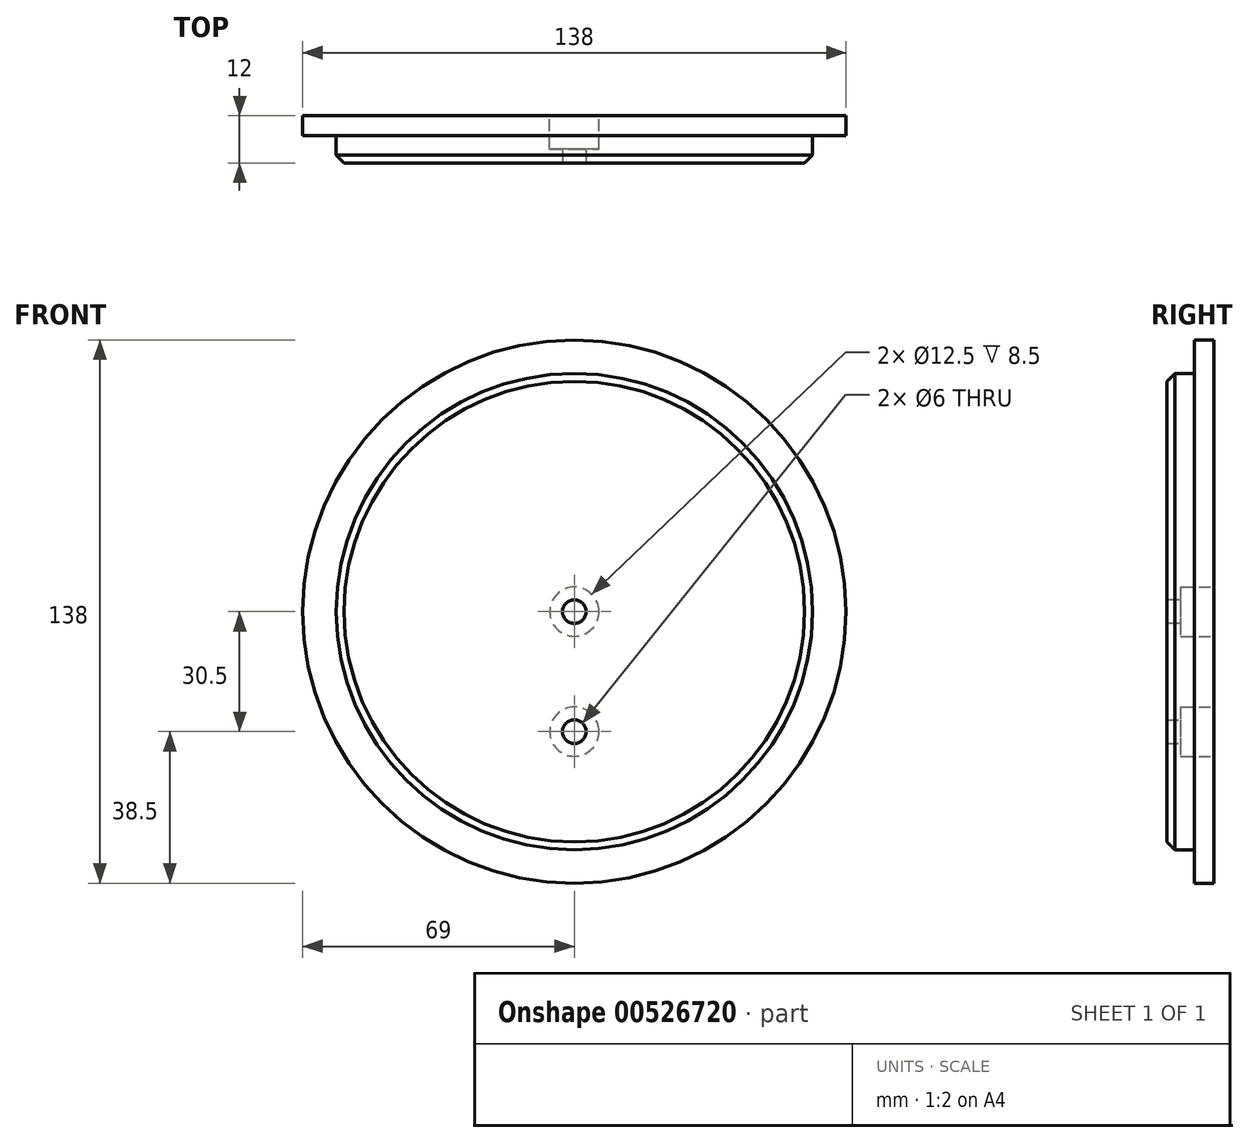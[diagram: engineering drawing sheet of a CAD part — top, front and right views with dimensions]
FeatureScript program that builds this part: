
annotation { "Feature Type Name" : "Feature", "Feature Type Description" : "" }
export const myFeature = defineFeature(function(context is Context, id is Id, definition is map)
    precondition{}
    {
        {
            var Q0;
            Q0=qCreatedBy(makeId("Front.planeOp"),FACE);
            var sketch = newSketch(context, id + "F0", { "sketchPlane" : qUnion([Q0])});
            skCircle(sketch, "E0", {"center": v(0, 0) * mm, "radius": 69 * mm});
            skSolve(sketch);
        }
        {
            var Q0;
            Q0=makeQuery(id+"F0.imprint","IMPRINT",FACE,{"disambiguationData":[TD([[makeQuery(id+"F0.imprint","IMPRINT",EDGE,{"derivedFrom":sQuery(id+"F0.wireOp",EDGE,"E0")}),1.0]])]});
            extrude(context, id + "F1", {"entities" : qUnion([Q0]), "depth" : 5 * mm, "offsetDistance" : 25 * mm});
        }
        {
            var Q0;
            Q0=makeQuery(id+"F1.opExtrude","CAP_FACE",FACE,{"disambiguationData":[OSD([sQuery(id+"F0.wireOp",EDGE,"E0")])],"isStart":false});
            var sketch = newSketch(context, id + "F2", { "sketchPlane" : qUnion([Q0])});
            skCircle(sketch, "E1", {"center": v(0, 0) * mm, "radius": 60.5 * mm});
            skSolve(sketch);
        }
        {
            var Q0;
            Q0=makeQuery(id+"F2.imprint","IMPRINT",FACE,{"disambiguationData":[TD([[makeQuery(id+"F2.imprint","IMPRINT",EDGE,{"derivedFrom":sQuery(id+"F2.wireOp",EDGE,"E1")}),1.0]])]});
            extrude(context, id + "F3", {"entities" : qUnion([Q0]), "operationType" : NewBodyOperationType.ADD, "depth" : (12 - 5) * mm, "offsetDistance" : 25 * mm});
        }
        {
            var Q0;
            Q0=makeQuery(id+"F1.opExtrude","CAP_FACE",FACE,{"disambiguationData":[OSD([sQuery(id+"F0.wireOp",EDGE,"E0")])],"isStart":true});
            var sketch = newSketch(context, id + "F4", { "sketchPlane" : qUnion([Q0])});
            skCircle(sketch, "E2", {"center": v(0, 0) * mm, "radius": 6.25 * mm});
            skSolve(sketch);
        }
        {
            var Q0;
            Q0=qSketchRegion(id+"F4",true);
            extrude(context, id + "F5", {"entities" : qUnion([Q0]), "operationType" : NewBodyOperationType.REMOVE, "oppositeDirection" : true, "depth" : 8.5 * mm, "offsetDistance" : 25 * mm});
        }
        {
            var Q0;
            Q0=makeQuery(id+"F3.opExtrude","CAP_FACE",FACE,{"disambiguationData":[OSD([sQuery(id+"F2.wireOp",EDGE,"E1")])],"isStart":false});
            var sketch = newSketch(context, id + "F6", { "sketchPlane" : qUnion([Q0])});
            skCircle(sketch, "E3", {"center": v(0, 0) * mm, "radius": 3 * mm});
            skSolve(sketch);
        }
        {
            var Q0;
            Q0=makeQuery(id+"F6.imprint","IMPRINT",FACE,{"disambiguationData":[TD([[makeQuery(id+"F6.imprint","IMPRINT",EDGE,{"derivedFrom":sQuery(id+"F6.wireOp",EDGE,"E3")}),1.0]])]});
            extrude(context, id + "F7", {"entities" : qUnion([Q0]), "operationType" : NewBodyOperationType.REMOVE, "oppositeDirection" : true, "depth" : 25 * mm, "offsetDistance" : 25 * mm});
        }
        {
            var Q0;
            Q0=makeQuery(id+"F1.opExtrude","CAP_FACE",FACE,{"disambiguationData":[OSD([sQuery(id+"F0.wireOp",EDGE,"E0")])],"isStart":true});
            var sketch = newSketch(context, id + "F8", { "sketchPlane" : qUnion([Q0])});
            skLineSegment(sketch, "E4", {"start": v(0, 0) * mm, "end": v(0, -61) * mm});
            skCircle(sketch, "E5", {"center": v(0, -30.5) * mm, "radius": 6.25 * mm});
            skSolve(sketch);
        }
        {
            var Q0;
            Q0 = qSketchRegion(id + "F8", true);
            extrude(context, id + "F9", {"entities" : qUnion([Q0]), "operationType" : NewBodyOperationType.REMOVE, "oppositeDirection" : true, "depth" : 8.5 * mm, "offsetDistance" : 25 * mm});
        }
        {
            var Q0;
            Q0=makeQuery(id+"F9.boolean.opBoolean","COPY",FACE,{"derivedFrom":makeQuery(id+"F9.opExtrude","CAP_FACE",FACE,{"disambiguationData":[OSD([sQuery(id+"F8.wireOp",EDGE,"E5")])],"isStart":false})});
            var sketch = newSketch(context, id + "F10", { "sketchPlane" : qUnion([Q0])});
            skCircle(sketch, "E6", {"center": v(0, -30.5) * mm, "radius": 3 * mm});
            skSolve(sketch);
        }
        {
            var Q0;
            Q0=makeQuery(id+"F10.imprint","IMPRINT",FACE,{"disambiguationData":[TD([[makeQuery(id+"F10.imprint","IMPRINT",EDGE,{"derivedFrom":sQuery(id+"F10.wireOp",EDGE,"E6")}),1.0]])]});
            extrude(context, id + "F11", {"entities" : qUnion([Q0]), "operationType" : NewBodyOperationType.REMOVE, "oppositeDirection" : true, "depth" : 25 * mm, "offsetDistance" : 25 * mm});
        }
        {
            var Q0;
            Q0=makeQuery(id+"F3.opExtrude","CAP_EDGE",EDGE,{"disambiguationData":[OSD([sQuery(id+"F2.wireOp",EDGE,"E1")])],"isStart":false});
            chamfer(context, id + "F12", {"entities" : qUnion([Q0]), "width" : 2 * mm, "tangentPropagation" : true});
        }
    });
